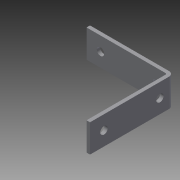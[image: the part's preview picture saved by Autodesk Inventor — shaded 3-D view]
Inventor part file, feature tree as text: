
AUTODESK INVENTOR PART (.ipt)
format: ipt  version: 2013 (Build 170138000, 138)  size: 162,816 bytes
history: native  units: in
note: dims shown in document units (in); Inventor stores cm internally (conversion verified against a paired STEP export)
features: sheet_metal_op x4, other x4, sketch x3
ambient origin geometry x8: Origin, YZ Plane, XZ Plane, XY Plane, X Axis, Y Axis, Z Axis, Center Point
bodies: Solid1 (feature_tree)
feature tree (11):
  sheet_metal_op  "Face1"
  sheet_metal_op  "Flange1"
  sketch  "Sketch1"  dims[d0=1.0in]
  other  "Plate1"
  sketch  "Sketch2"  dims[d1=3.0in]
  other  "Plate2"
  sheet_metal_op  "Bend1"
  sheet_metal_op  "Corner1"
  sketch  "Sketch3"  dims[d2=0.266in d3=0.266in d4=0.5in d5=0.5in d6=0.5in d7=0.5in d8=0.125in d9=0.125in d10=0.0625in d11=0.25in d12=0.125in d13=3.0in d14=90.0deg d15=0.05in d16=0.5in d17=0.125in d18=0.125in d19=0.266in d20=0.266in d22=0.5in d23=0.5in d24=0.5in d25=0.125in d26=0.0in d27=2.0in]
  other  "Cut1"
  other  "Definition1"
